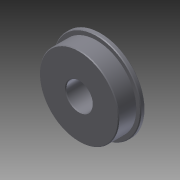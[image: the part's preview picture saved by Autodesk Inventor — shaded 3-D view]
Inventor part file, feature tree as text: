
AUTODESK INVENTOR PART (.ipt)
format: ipt  version: 2014 SP1 (Build 180222100, 222)  size: 108,032 bytes
history: native  units: in
note: dims shown in document units (in); Inventor stores cm internally (conversion verified against a paired STEP export)
features: extrude x2, sketch x1, chamfer x1
ambient origin geometry x8: Origin, YZ Plane, XZ Plane, XY Plane, X Axis, Y Axis, Z Axis, Center Point
bodies: Solid1 (feature_tree)
feature tree (4):
  sketch  "Sketch1"  dims[d0=1.125in d1=0.375in d2=1.25in d3=0.251in d4=0.0in d5=0.063in d6=0.0in d7=0.01in d8=0.125in d9=45.0deg]
  extrude  "Extrusion1"  Depth=0.063in
  extrude  "Extrusion2"  Depth=0.063in
  chamfer  "Chamfer1"  Distance=0.251in
